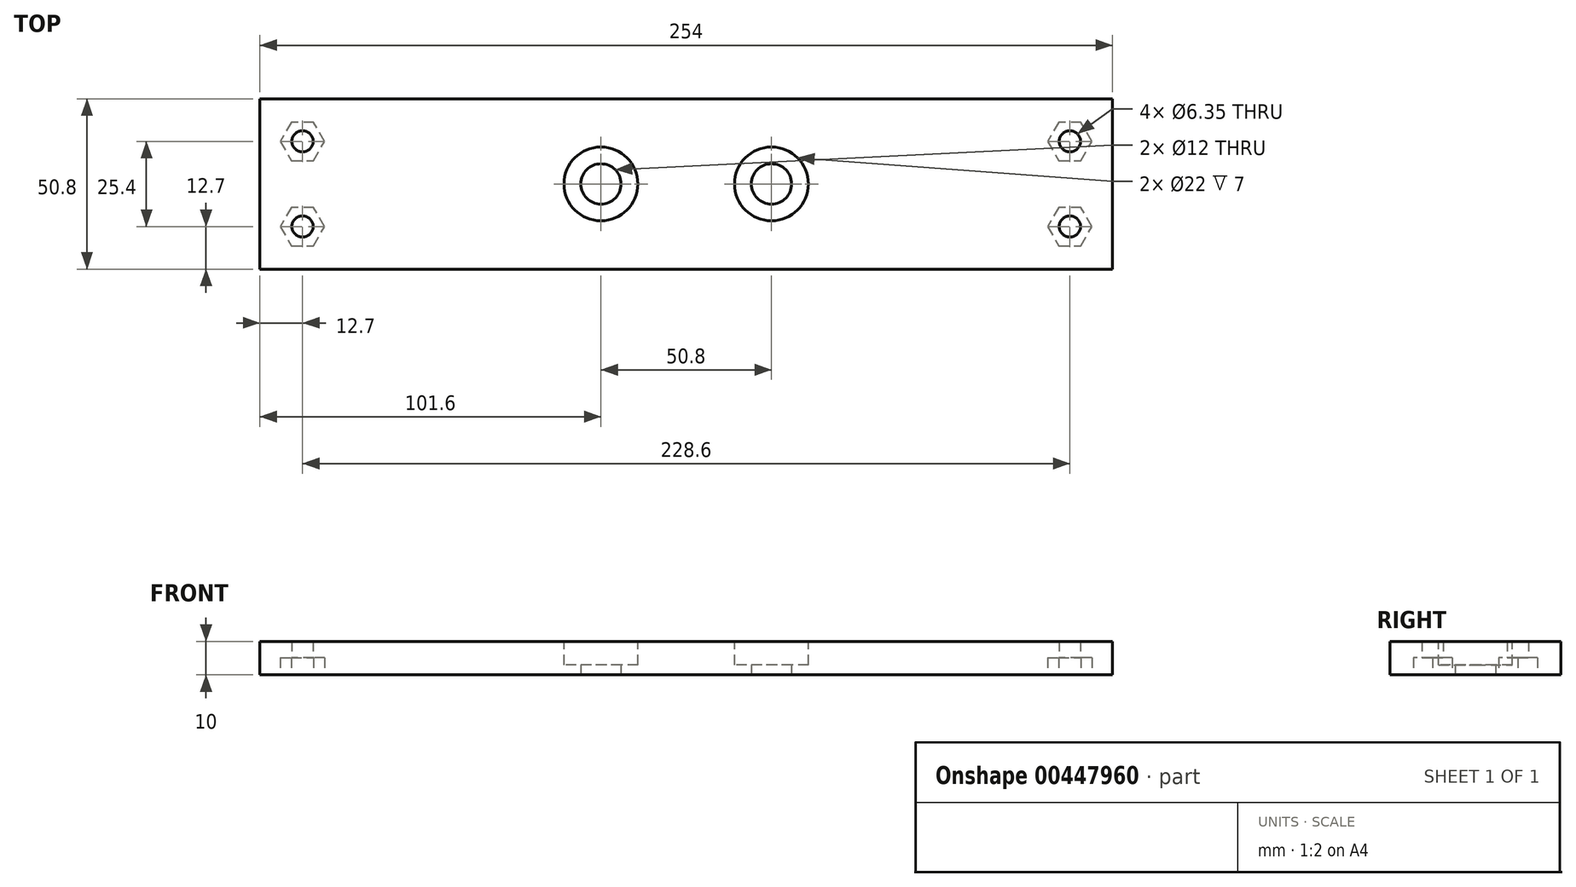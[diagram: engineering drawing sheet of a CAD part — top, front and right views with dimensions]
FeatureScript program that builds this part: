
annotation { "Feature Type Name" : "Feature", "Feature Type Description" : "" }
export const myFeature = defineFeature(function(context is Context, id is Id, definition is map)
    precondition{}
    {
        {
            var Q0;
            Q0=qCreatedBy(makeId("Top.planeOp"),FACE);
            var sketch = newSketch(context, id + "F0", { "sketchPlane" : qUnion([Q0])});
            skLineSegment(sketch, "E0.bottom", {"start": v(127, 25.4) * mm, "end": v(-127, 25.4) * mm});
            skLineSegment(sketch, "E0.top", {"start": v(127, -25.4) * mm, "end": v(-127, -25.4) * mm});
            skLineSegment(sketch, "E0.left", {"start": v(127, 25.4) * mm, "end": v(127, -25.4) * mm});
            skLineSegment(sketch, "E0.right", {"start": v(-127, 25.4) * mm, "end": v(-127, -25.4) * mm});
            skPoint(sketch, "E0.middle", {"position": v(0, 0) * mm});
            skCircle(sketch, "E1", {"center": v(25.4, 0) * mm, "radius": 25.4 * mm, "construction": true});
            skCircle(sketch, "E2", {"center": v(-25.4, 0) * mm, "radius": 25.4 * mm, "construction": true});
            skCircle(sketch, "E3", {"center": v(25.4, 0) * mm, "radius": 6 * mm});
            skCircle(sketch, "E4", {"center": v(-25.4, 0) * mm, "radius": 6 * mm});
            skCircle(sketch, "E5", {"center": v(-114.3, 12.7) * mm, "radius": 3.18 * mm});
            skCircle(sketch, "E6", {"center": v(-114.3, -12.7) * mm, "radius": 3.18 * mm});
            skCircle(sketch, "E7", {"center": v(114.3, -12.7) * mm, "radius": 3.18 * mm});
            skCircle(sketch, "E8", {"center": v(114.3, 12.7) * mm, "radius": 3.18 * mm});
            skSolve(sketch);
        }
        {
            var Q0;
            Q0=makeQuery(id+"F0.imprint","IMPRINT",FACE,{"disambiguationData":[TD([[makeQuery(id+"F0.imprint","IMPRINT",EDGE,{"derivedFrom":sQuery(id+"F0.wireOp",EDGE,"E0.bottom")}),1.0]])]});
            extrude(context, id + "F1", {"entities" : qUnion([Q0]), "depth" : 10 * mm});
        }
        {
            var Q0;
            Q0=makeQuery(id+"F1.opExtrude","CAP_FACE",FACE,{"disambiguationData":[OSD([sQuery(id+"F0.wireOp",EDGE,"E0.bottom"),sQuery(id+"F0.wireOp",EDGE,"E0.top"),sQuery(id+"F0.wireOp",EDGE,"E0.left"),sQuery(id+"F0.wireOp",EDGE,"E0.right"),sQuery(id+"F0.wireOp",EDGE,"E3"),sQuery(id+"F0.wireOp",EDGE,"E4"),sQuery(id+"F0.wireOp",EDGE,"E5"),sQuery(id+"F0.wireOp",EDGE,"E6"),sQuery(id+"F0.wireOp",EDGE,"E7"),sQuery(id+"F0.wireOp",EDGE,"E8")])],"isStart":false});
            var sketch = newSketch(context, id + "F2", { "sketchPlane" : qUnion([Q0])});
            skCircle(sketch, "E9", {"center": v(-25.4, 0) * mm, "radius": 11 * mm});
            skCircle(sketch, "E10", {"center": v(25.4, 0) * mm, "radius": 11 * mm});
            skSolve(sketch);
        }
        {
            var Q0;
            Q0=makeQuery(id+"F2.imprint","IMPRINT",FACE,{"disambiguationData":[TD([[makeQuery(id+"F2.imprint","IMPRINT",EDGE,{"derivedFrom":sQuery(id+"F2.wireOp",EDGE,"E9")}),1.0]])]});
            var Q1;
            Q1=makeQuery(id+"F2.imprint","IMPRINT",FACE,{"disambiguationData":[TD([[makeQuery(id+"F2.imprint","IMPRINT",EDGE,{"derivedFrom":sQuery(id+"F2.wireOp",EDGE,"E10")}),1.0]])]});
            extrude(context, id + "F3", {"entities" : qUnion([Q0, Q1]), "operationType" : NewBodyOperationType.REMOVE, "oppositeDirection" : true, "depth" : 7 * mm});
        }
        {
            var Q0;
            Q0=makeQuery(id+"F1.opExtrude","CAP_FACE",FACE,{"disambiguationData":[OSD([sQuery(id+"F0.wireOp",EDGE,"E0.bottom"),sQuery(id+"F0.wireOp",EDGE,"E0.top"),sQuery(id+"F0.wireOp",EDGE,"E0.left"),sQuery(id+"F0.wireOp",EDGE,"E0.right"),sQuery(id+"F0.wireOp",EDGE,"E3"),sQuery(id+"F0.wireOp",EDGE,"E4"),sQuery(id+"F0.wireOp",EDGE,"E5"),sQuery(id+"F0.wireOp",EDGE,"E6"),sQuery(id+"F0.wireOp",EDGE,"E7"),sQuery(id+"F0.wireOp",EDGE,"E8")])],"isStart":true});
            var sketch = newSketch(context, id + "F4", { "sketchPlane" : qUnion([Q0])});
            skCircle(sketch, "E11.cCircle", {"center": v(-114.3, 12.7) * mm, "radius": 5.72 * mm, "construction": true});
            skLineSegment(sketch, "E11.0", {"start": v(-117.6, 18.42) * mm, "end": v(-111, 18.42) * mm});
            skLineSegment(sketch, "E11.1", {"start": v(-111, 18.42) * mm, "end": v(-107.7, 12.7) * mm});
            skLineSegment(sketch, "E11.2", {"start": v(-107.7, 12.7) * mm, "end": v(-111, 6.99) * mm});
            skLineSegment(sketch, "E11.3", {"start": v(-111, 6.99) * mm, "end": v(-117.6, 6.99) * mm});
            skLineSegment(sketch, "E11.4", {"start": v(-117.6, 6.99) * mm, "end": v(-120.9, 12.7) * mm});
            skLineSegment(sketch, "E11.5", {"start": v(-120.9, 12.7) * mm, "end": v(-117.6, 18.42) * mm});
            skPoint(sketch, "E11.0.midPoint", {"position": v(-114.3, 18.42) * mm});
            skCircle(sketch, "E12.cCircle", {"center": v(-114.3, -12.7) * mm, "radius": 5.72 * mm, "construction": true});
            skLineSegment(sketch, "E12.0", {"start": v(-117.6, -6.99) * mm, "end": v(-111, -6.99) * mm});
            skLineSegment(sketch, "E12.1", {"start": v(-111, -6.99) * mm, "end": v(-107.7, -12.7) * mm});
            skLineSegment(sketch, "E12.2", {"start": v(-107.7, -12.7) * mm, "end": v(-111, -18.42) * mm});
            skLineSegment(sketch, "E12.3", {"start": v(-111, -18.42) * mm, "end": v(-117.6, -18.42) * mm});
            skLineSegment(sketch, "E12.4", {"start": v(-117.6, -18.42) * mm, "end": v(-120.9, -12.7) * mm});
            skLineSegment(sketch, "E12.5", {"start": v(-120.9, -12.7) * mm, "end": v(-117.6, -6.99) * mm});
            skPoint(sketch, "E12.0.midPoint", {"position": v(-114.3, -6.99) * mm});
            skCircle(sketch, "E13.cCircle", {"center": v(114.3, 12.7) * mm, "radius": 5.72 * mm, "construction": true});
            skLineSegment(sketch, "E13.0", {"start": v(111, 18.42) * mm, "end": v(117.6, 18.42) * mm});
            skLineSegment(sketch, "E13.1", {"start": v(117.6, 18.42) * mm, "end": v(120.9, 12.7) * mm});
            skLineSegment(sketch, "E13.2", {"start": v(120.9, 12.7) * mm, "end": v(117.6, 6.99) * mm});
            skLineSegment(sketch, "E13.3", {"start": v(117.6, 6.99) * mm, "end": v(111, 6.99) * mm});
            skLineSegment(sketch, "E13.4", {"start": v(111, 6.99) * mm, "end": v(107.7, 12.7) * mm});
            skLineSegment(sketch, "E13.5", {"start": v(107.7, 12.7) * mm, "end": v(111, 18.42) * mm});
            skPoint(sketch, "E13.0.midPoint", {"position": v(114.3, 18.41) * mm});
            skCircle(sketch, "E14.cCircle", {"center": v(114.3, -12.7) * mm, "radius": 5.72 * mm, "construction": true});
            skLineSegment(sketch, "E14.0", {"start": v(111, -6.99) * mm, "end": v(117.6, -6.99) * mm});
            skLineSegment(sketch, "E14.1", {"start": v(117.6, -6.98) * mm, "end": v(120.9, -12.7) * mm});
            skLineSegment(sketch, "E14.2", {"start": v(120.9, -12.7) * mm, "end": v(117.6, -18.42) * mm});
            skLineSegment(sketch, "E14.3", {"start": v(117.6, -18.42) * mm, "end": v(111, -18.42) * mm});
            skLineSegment(sketch, "E14.4", {"start": v(111, -18.42) * mm, "end": v(107.7, -12.7) * mm});
            skLineSegment(sketch, "E14.5", {"start": v(107.7, -12.7) * mm, "end": v(111, -6.99) * mm});
            skPoint(sketch, "E14.0.midPoint", {"position": v(114.3, -6.99) * mm});
            skSolve(sketch);
        }
        {
            var Q0;
            Q0=makeQuery(id+"F4.imprint","IMPRINT",FACE,{"disambiguationData":[TD([[makeQuery(id+"F4.imprint","IMPRINT",EDGE,{"derivedFrom":sQuery(id+"F4.wireOp",EDGE,"E11.0")}),-1.0]])]});
            var Q1;
            Q1=makeQuery(id+"F4.imprint","IMPRINT",FACE,{"disambiguationData":[TD([[makeQuery(id+"F4.imprint","IMPRINT",EDGE,{"derivedFrom":sQuery(id+"F4.wireOp",EDGE,"E12.0")}),-1.0]])]});
            var Q2;
            Q2=makeQuery(id+"F4.imprint","IMPRINT",FACE,{"disambiguationData":[TD([[makeQuery(id+"F4.imprint","IMPRINT",EDGE,{"derivedFrom":sQuery(id+"F4.wireOp",EDGE,"E14.0")}),-1.0]])]});
            var Q3;
            Q3=makeQuery(id+"F4.imprint","IMPRINT",FACE,{"disambiguationData":[TD([[makeQuery(id+"F4.imprint","IMPRINT",EDGE,{"derivedFrom":sQuery(id+"F4.wireOp",EDGE,"E13.0")}),-1.0]])]});
            extrude(context, id + "F5", {"entities" : qUnion([Q0, Q1, Q2, Q3]), "operationType" : NewBodyOperationType.REMOVE, "oppositeDirection" : true, "depth" : 5.08 * mm});
        }
    });
